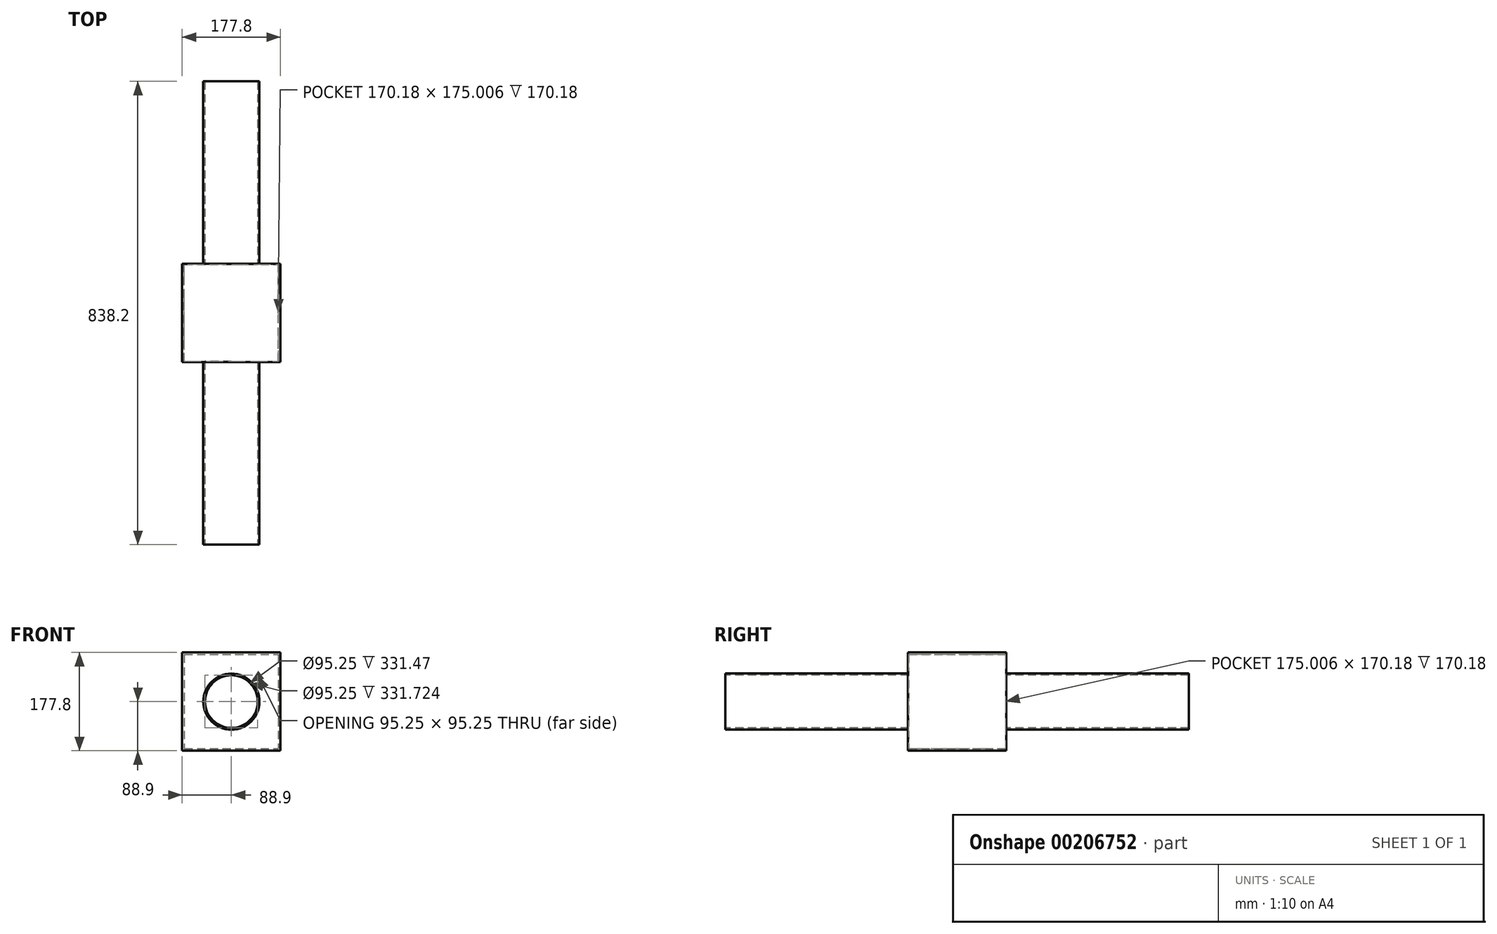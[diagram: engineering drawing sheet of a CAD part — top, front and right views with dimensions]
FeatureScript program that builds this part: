
annotation { "Feature Type Name" : "Feature", "Feature Type Description" : "" }
export const myFeature = defineFeature(function(context is Context, id is Id, definition is map)
    precondition{}
    {
        {
            var Q0;
            Q0=qCreatedBy(makeId("Front.planeOp"),FACE);
            var sketch = newSketch(context, id + "F0", { "sketchPlane" : qUnion([Q0])});
            skCircle(sketch, "E0", {"center": v(0, 0) * mm, "radius": 50.8 * mm});
            skSolve(sketch);
        }
        {
            var Q0;
            Q0 = qSketchRegion(id + "F0", true);
            extrude(context, id + "F1", {"entities" : qUnion([Q0]), "depth" : 330.2 * mm, "hasSecondDirection" : true, "secondDirectionOppositeDirection" : true, "secondDirectionDepth" : 508 * mm});
        }
        {
            var Q0;
            Q0=makeQuery(id+"F1.opExtrude","CAP_FACE",FACE,{"disambiguationData":[OSD([sQuery(id+"F0.wireOp",EDGE,"E0")])],"isStart":false});
            var sketch = newSketch(context, id + "F2", { "sketchPlane" : qUnion([Q0])});
            skCircle(sketch, "E1", {"center": v(0, 0) * mm, "radius": 47.63 * mm});
            skSolve(sketch);
        }
        {
            var Q0;
            Q0=qCreatedBy(makeId("Front.planeOp"),FACE);
            var sketch = newSketch(context, id + "F3", { "sketchPlane" : qUnion([Q0])});
            skLineSegment(sketch, "E2.bottom", {"start": v(-88.9, 88.9) * mm, "end": v(88.9, 88.9) * mm});
            skLineSegment(sketch, "E2.top", {"start": v(-88.9, -88.9) * mm, "end": v(88.9, -88.9) * mm});
            skLineSegment(sketch, "E2.left", {"start": v(-88.9, 88.9) * mm, "end": v(-88.9, -88.9) * mm});
            skLineSegment(sketch, "E2.right", {"start": v(88.9, 88.9) * mm, "end": v(88.9, -88.9) * mm});
            skPoint(sketch, "E2.middle", {"position": v(0, 0) * mm});
            skSolve(sketch);
        }
        {
            var Q0;
            Q0 = qSketchRegion(id + "F3", true);
            extrude(context, id + "F4", {"entities" : qUnion([Q0]), "operationType" : NewBodyOperationType.ADD, "oppositeDirection" : true, "depth" : 177.8 * mm});
        }
        {
            var Q0;
            Q0=makeQuery(id+"F4.opExtrude","CAP_FACE",FACE,{"disambiguationData":[OSD([sQuery(id+"F3.wireOp",EDGE,"E2.bottom"),sQuery(id+"F3.wireOp",EDGE,"E2.top"),sQuery(id+"F3.wireOp",EDGE,"E2.left"),sQuery(id+"F3.wireOp",EDGE,"E2.right")])],"isStart":false});
            var sketch = newSketch(context, id + "F5", { "sketchPlane" : qUnion([Q0])});
            skLineSegment(sketch, "E3.bottom", {"start": v(85.1, 85.1) * mm, "end": v(-85.1, 85.1) * mm});
            skLineSegment(sketch, "E3.top", {"start": v(85.1, -85.1) * mm, "end": v(-85.1, -85.1) * mm});
            skLineSegment(sketch, "E3.left", {"start": v(85.1, 85.1) * mm, "end": v(85.1, -85.1) * mm});
            skLineSegment(sketch, "E3.right", {"start": v(-85.1, 85.1) * mm, "end": v(-85.1, -85.1) * mm});
            skPoint(sketch, "E3.middle", {"position": v(0, 0) * mm});
            skSolve(sketch);
        }
        {
            var Q0;
            Q0 = qSketchRegion(id + "F5", true);
            extrude(context, id + "F6", {"entities" : qUnion([Q0]), "operationType" : NewBodyOperationType.REMOVE, "oppositeDirection" : true, "depth" : 176.28 * mm, "hasSecondDirection" : true, "secondDirectionOppositeDirection" : true, "secondDirectionDepth" : 1.27 * mm});
        }
        {
            var Q0;
            Q0=makeQuery(id+"F2.imprint","IMPRINT",FACE,{"disambiguationData":[TD([[makeQuery(id+"F2.imprint","IMPRINT",EDGE,{"derivedFrom":sQuery(id+"F2.wireOp",EDGE,"E1")}),1.0]])]});
            var Q1;
            Q1=sQuery(id+"F2.wireOp",EDGE,"E1");
            extrude(context, id + "F7", {"entities" : qUnion([Q0]), "operationType" : NewBodyOperationType.REMOVE, "surfaceEntities" : qUnion([Q1]), "oppositeDirection" : true, "depth" : 914.4 * mm});
        }
    });
